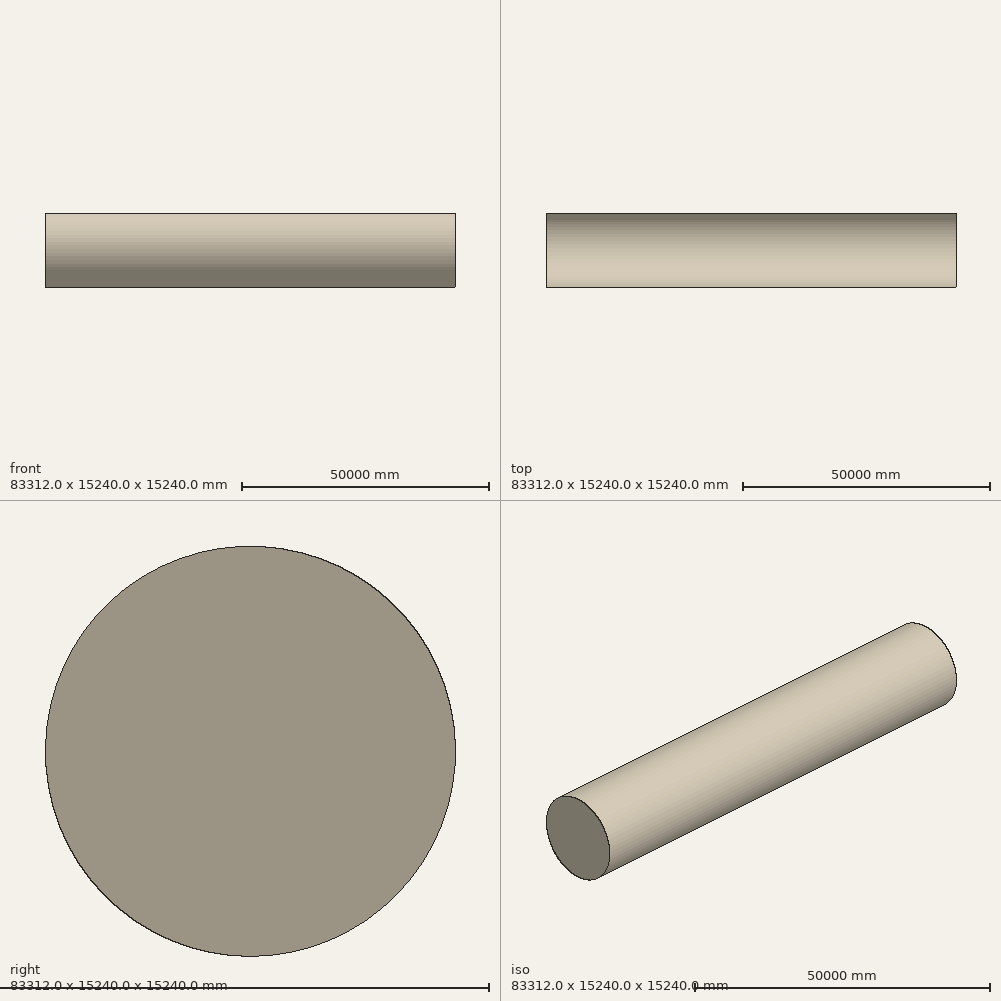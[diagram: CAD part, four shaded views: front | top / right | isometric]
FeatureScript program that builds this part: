
annotation { "Feature Type Name" : "Feature", "Feature Type Description" : "" }
export const myFeature = defineFeature(function(context is Context, id is Id, definition is map)
    precondition{}
    {
        {
            var Q0;
            Q0=qCreatedBy(makeId("Right.planeOp"),FACE);
            var sketch = newSketch(context, id + "F0", { "sketchPlane" : qUnion([Q0])});
            skCircle(sketch, "E0", {"center": v(0, 0) * mm, "radius": 7620 * mm});
            skSolve(sketch);
        }
        {
            var Q0;
            Q0=makeQuery(id+"F0.imprint","IMPRINT",FACE,{"disambiguationData":[TD([[makeQuery(id+"F0.imprint","IMPRINT",EDGE,{"derivedFrom":sQuery(id+"F0.wireOp",EDGE,"E0")}),1.0]])]});
            extrude(context, id + "F1", {"entities" : qUnion([Q0]), "oppositeDirection" : true, "depth" : 83312 * mm, "offsetDistance" : 25.4 * mm});
        }
        {
            var Q0;
            Q0=makeQuery(id+"F1.opExtrude","CAP_FACE",FACE,{"disambiguationData":[OSD([sQuery(id+"F0.wireOp",EDGE,"E0")])],"isStart":true});
            extrude(context, id + "F2", {"entities" : qUnion([Q0]), "operationType" : NewBodyOperationType.ADD, "oppositeDirection" : true, "depth" : 29210 * mm, "offsetDistance" : 25.4 * mm});
        }
    });
